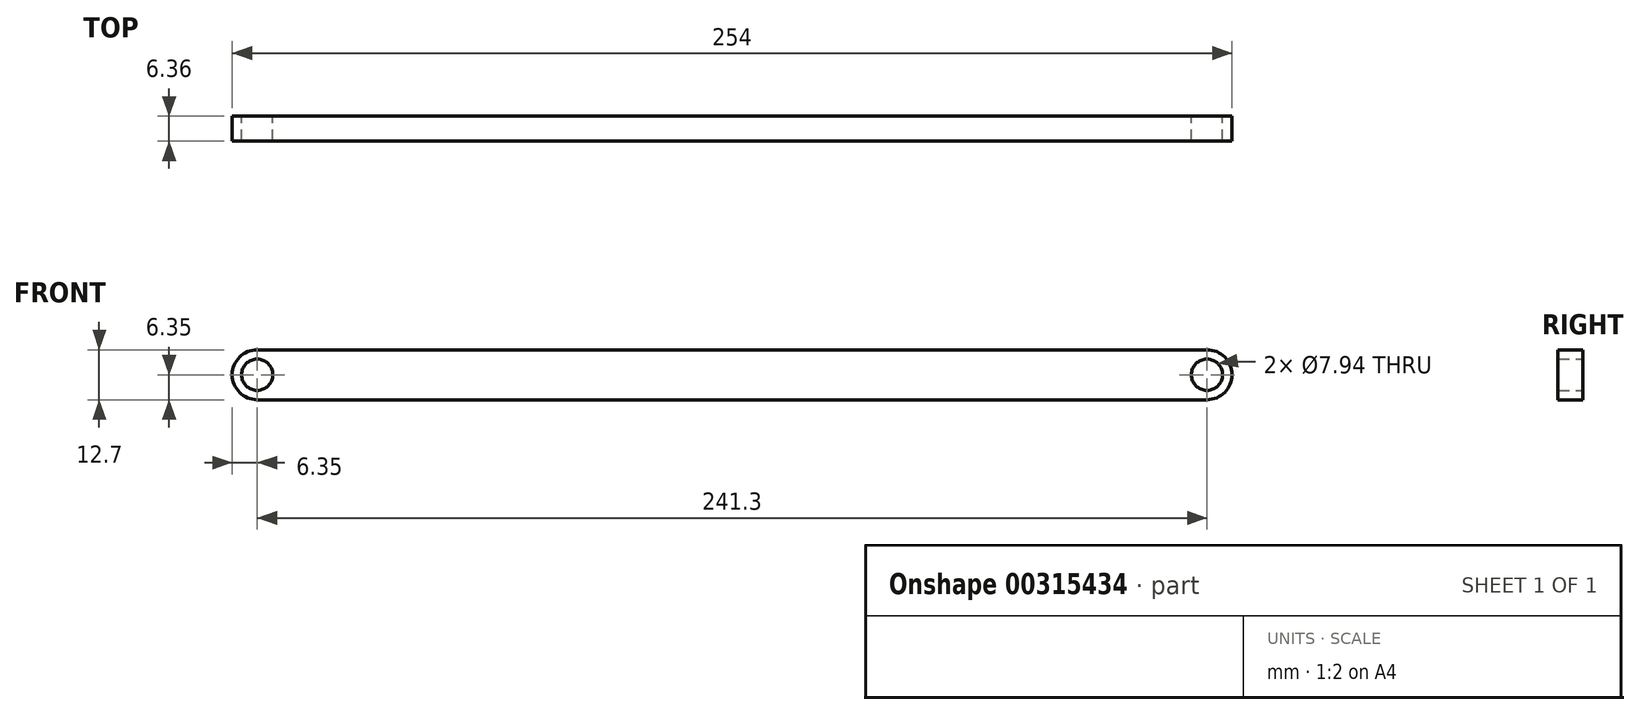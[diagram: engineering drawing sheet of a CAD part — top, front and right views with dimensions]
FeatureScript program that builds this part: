
annotation { "Feature Type Name" : "Feature", "Feature Type Description" : "" }
export const myFeature = defineFeature(function(context is Context, id is Id, definition is map)
    precondition{}
    {
        {
            var Q0;
            Q0=qCreatedBy(makeId("Front.planeOp"),FACE);
            var sketch = newSketch(context, id + "F0", { "sketchPlane" : qUnion([Q0])});
            skLineSegment(sketch, "E0.bottom", {"start": v(-120.65, 6.35) * mm, "end": v(120.65, 6.35) * mm});
            skLineSegment(sketch, "E0.top", {"start": v(-120.65, -6.35) * mm, "end": v(120.65, -6.35) * mm});
            skLineSegment(sketch, "E0.left", {"start": v(-127, 0) * mm, "end": v(-127, 0) * mm});
            skLineSegment(sketch, "E0.right", {"start": v(127, 0) * mm, "end": v(127, 0) * mm});
            skPoint(sketch, "E0.middle", {"position": v(0, 0) * mm});
            skPoint(sketch, "E1.visualSharp", {"position": v(-127, 6.35) * mm});
            skArc(sketch, "E1.filletArc", {"start": v(-120.65, 6.35) * mm, "mid": v(-125.14, 4.5) * mm, "end": v(-127, 0) * mm});
            skPoint(sketch, "E2.visualSharp", {"position": v(-127, -6.35) * mm});
            skArc(sketch, "E2.filletArc", {"start": v(-127, 0) * mm, "mid": v(-125.14, -4.5) * mm, "end": v(-120.65, -6.35) * mm});
            skPoint(sketch, "E3.visualSharp", {"position": v(127, 6.35) * mm});
            skArc(sketch, "E3.filletArc", {"start": v(127, 0) * mm, "mid": v(125.14, 4.5) * mm, "end": v(120.65, 6.35) * mm});
            skPoint(sketch, "E4.visualSharp", {"position": v(127, -6.35) * mm});
            skArc(sketch, "E4.filletArc", {"start": v(120.65, -6.35) * mm, "mid": v(125.14, -4.5) * mm, "end": v(127, 0) * mm});
            skCircle(sketch, "E5", {"center": v(-120.65, 0) * mm, "radius": 3.97 * mm});
            skLineSegment(sketch, "E6", {"start": v(0, 0) * mm, "end": v(0, 23.17) * mm, "construction": true});
            skCircle(sketch, "E7.MirrorC", {"center": v(120.65, 0) * mm, "radius": 3.97 * mm});
            skSolve(sketch);
        }
        {
            var Q0;
            Q0 = qSketchRegion(id + "F0", true);
            extrude(context, id + "F1", {"entities" : qUnion([Q0]), "endBound" : BoundingType.SYMMETRIC, "depth" : 6.35 * mm});
        }
    });
